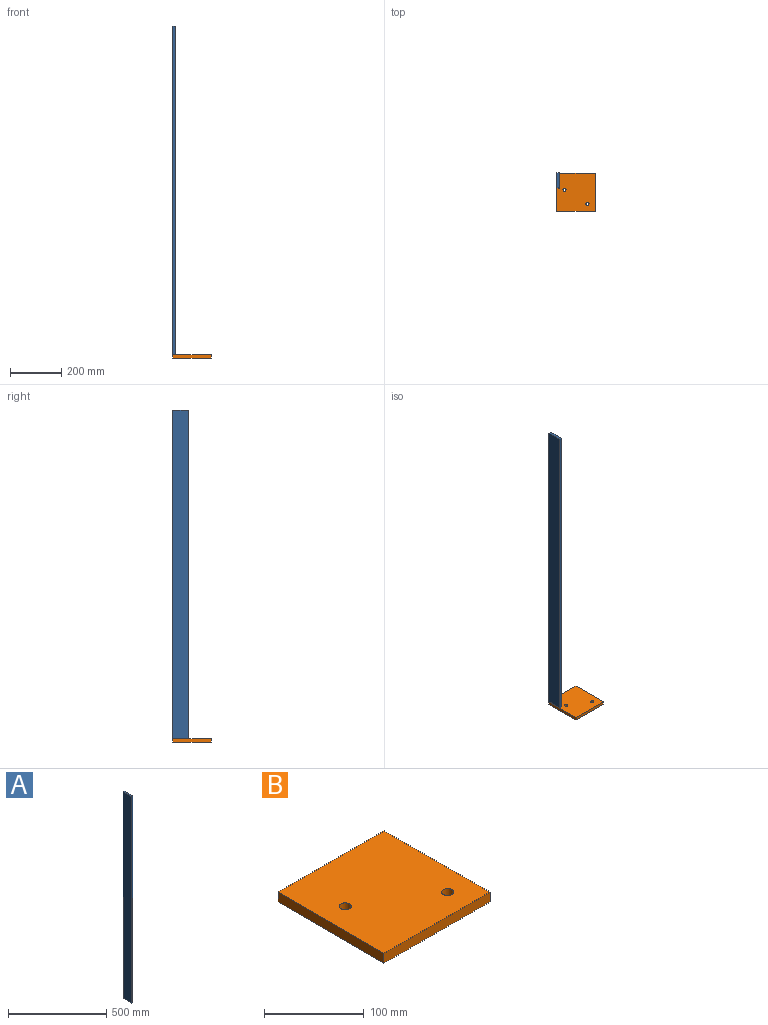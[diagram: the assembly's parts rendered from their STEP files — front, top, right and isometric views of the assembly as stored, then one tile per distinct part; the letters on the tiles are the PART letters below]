
ASSEMBLY  parts=2 mates=1
PART A: 6 faces, bbox 10x60x1288 mm
  f0: plane 1288x60mm, normal (-1,0,0), area 77280mm2, adj f1,f3,f4,f5
  f1: plane 1288x10mm, normal (0,-1,0), area 12880mm2, adj f0,f2,f4,f5
  f2: plane 1288x60mm, normal (1,0,0), area 77280mm2, adj f1,f3,f4,f5
  f3: plane 1288x10mm, normal (0,1,0), area 12880mm2, adj f0,f2,f4,f5
  f4: plane 60x10mm, normal (0,0,1), area 600mm2, adj f0,f1,f2,f3
  f5: plane 60x10mm, normal (0,0,-1), area 600mm2, adj f0,f1,f2,f3
PART B: 8 faces, bbox 150x150x12 mm
  f0: plane 150x12mm, normal (1,0,0), area 1800mm2, adj f1,f3,f4,f5
  f1: plane 150x12mm, normal (0,1,0), area 1800mm2, adj f0,f2,f4,f5
  f2: plane 150x12mm, normal (-1,0,0), area 1800mm2, adj f1,f3,f4,f5
  f3: plane 150x12mm, normal (0,-1,0), area 1800mm2, adj f0,f2,f4,f5
  f4: plane 150x150mm, normal (0,0,1), area 22273.8mm2, adj f0,f1,f2,f3,f6,f7
  f5: plane 150x150mm, normal (0,0,-1), area 22273.8mm2, adj f0,f1,f2,f3,f6,f7
  f6: cylinder r=6mm len=12mm, axis (0,0,1), area 452.4mm2, adj f4,f5
  f7: cylinder r=6mm len=12mm, axis (0,0,1), area 452.4mm2, adj f4,f5
PLACE A t=(-85.93,9.65,5.84)mm
PLACE B t=(-10.93,-5.35,-6.16)mm
MATE fastened A.f5 <-> B.f4  axis (0,0,1) through (-80.93,39.65,5.84)mm
